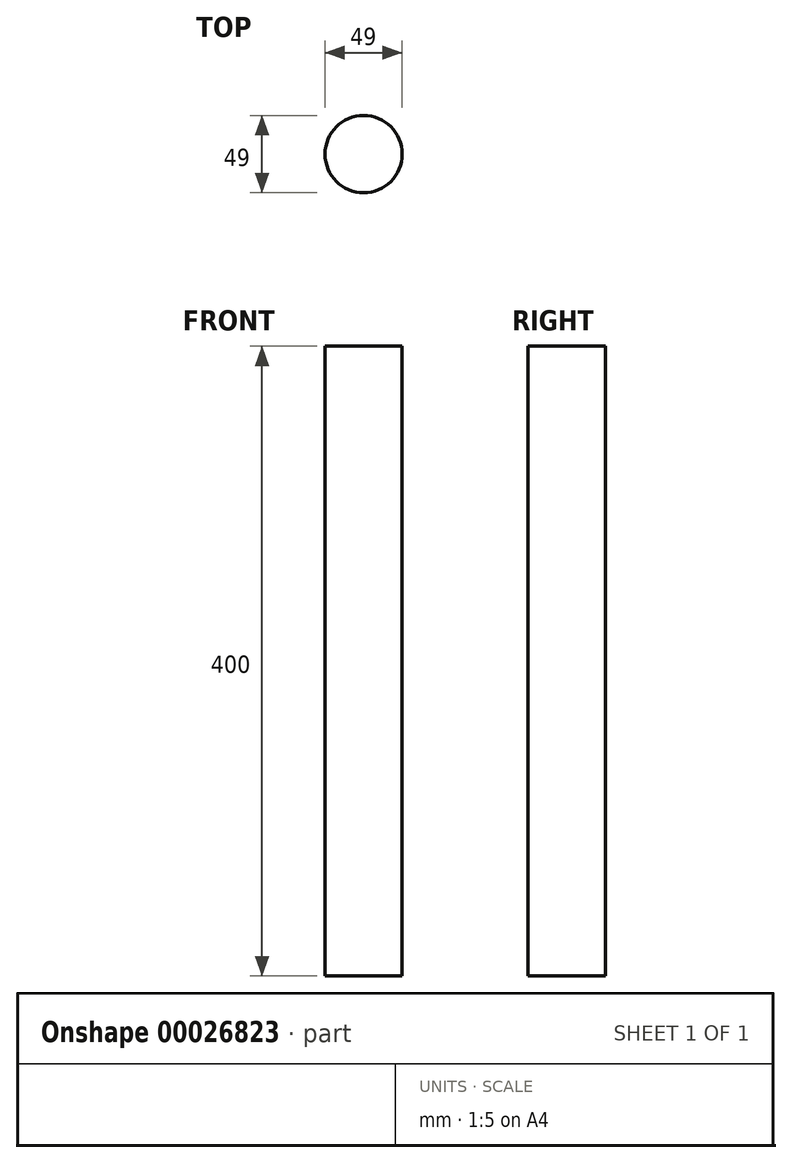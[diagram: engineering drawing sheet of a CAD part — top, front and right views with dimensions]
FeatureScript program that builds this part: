
annotation { "Feature Type Name" : "Feature", "Feature Type Description" : "" }
export const myFeature = defineFeature(function(context is Context, id is Id, definition is map)
    precondition{}
    {
        {
            var Q0;
            Q0=qCreatedBy(makeId("Top.planeOp"),FACE);
            var sketch = newSketch(context, id + "F0", { "sketchPlane" : qUnion([Q0])});
            skCircle(sketch, "E0", {"center": v(-11.09, -1.22) * mm, "radius": 24.5 * mm});
            skSolve(sketch);
        }
        {
            var Q0;
            Q0=makeQuery(id+"F0.imprint","IMPRINT",FACE,{"disambiguationData":[TD([[makeQuery(id+"F0.imprint","IMPRINT",EDGE,{"derivedFrom":sQuery(id+"F0.wireOp",EDGE,"E0")}),1.0]])]});
            extrude(context, id + "F1", {"entities" : qUnion([Q0]), "depth" : 400 * mm});
        }
    });
